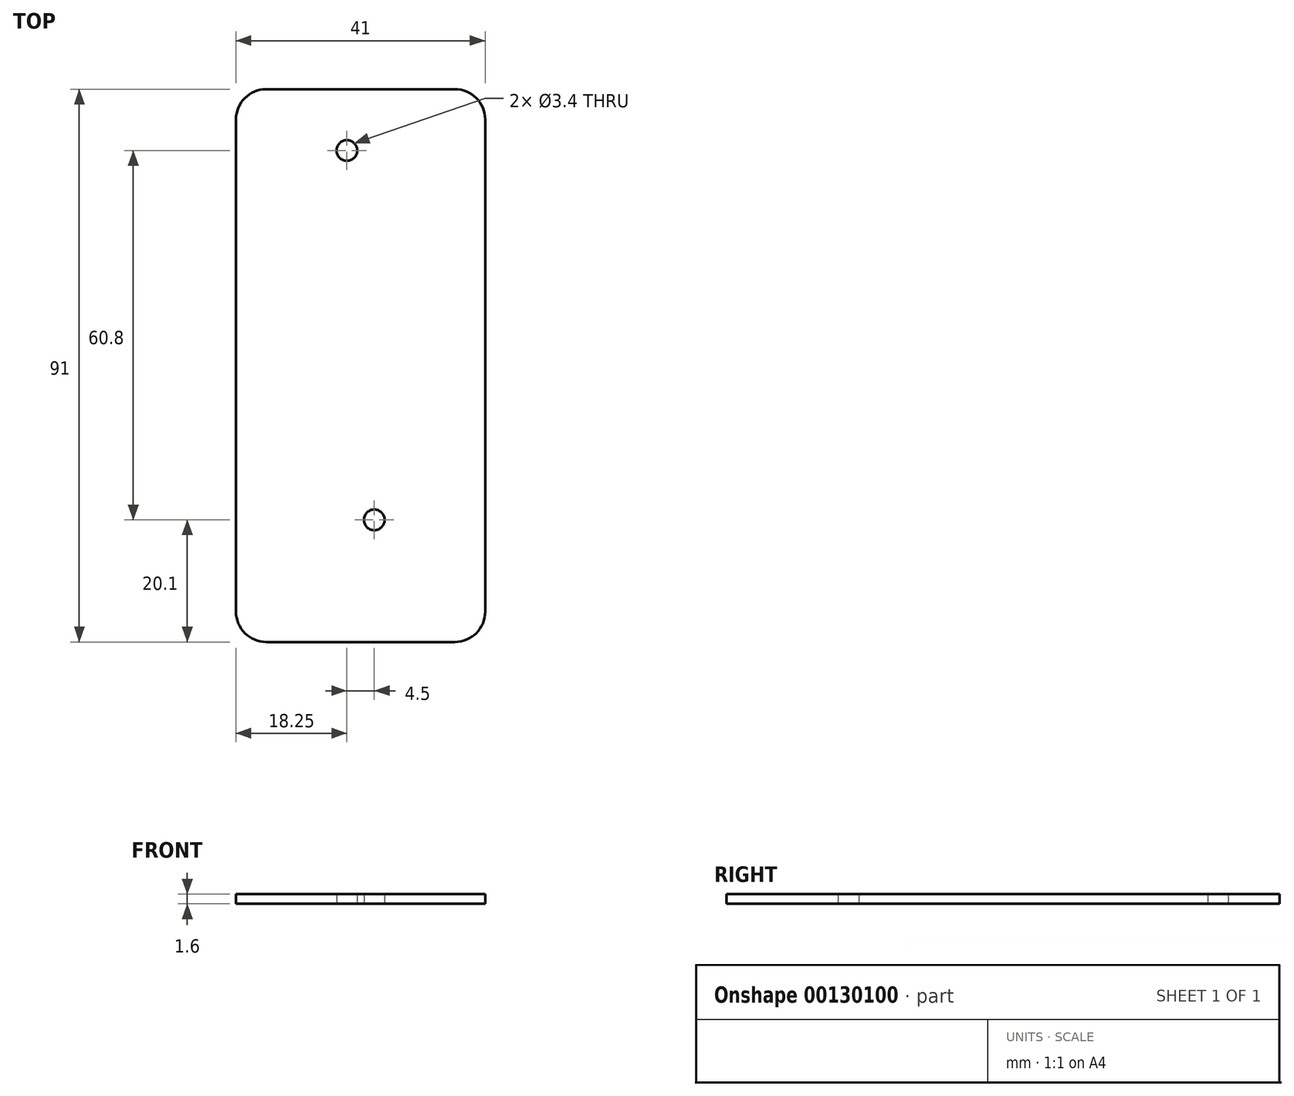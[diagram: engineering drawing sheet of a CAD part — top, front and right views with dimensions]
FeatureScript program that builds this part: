
annotation { "Feature Type Name" : "Feature", "Feature Type Description" : "" }
export const myFeature = defineFeature(function(context is Context, id is Id, definition is map)
    precondition{}
    {
        {
            var Q0;
            Q0=qCreatedBy(makeId("Top.planeOp"),FACE);
            var sketch = newSketch(context, id + "F0", { "sketchPlane" : qUnion([Q0])});
            skLineSegment(sketch, "E0.bottom", {"start": v(20.5, 45.5) * mm, "end": v(-20.5, 45.5) * mm});
            skLineSegment(sketch, "E0.top", {"start": v(20.5, -45.5) * mm, "end": v(-20.5, -45.5) * mm});
            skLineSegment(sketch, "E0.left", {"start": v(20.5, 45.5) * mm, "end": v(20.5, -45.5) * mm});
            skLineSegment(sketch, "E0.right", {"start": v(-20.5, 45.5) * mm, "end": v(-20.5, -45.5) * mm});
            skPoint(sketch, "E0.middle", {"position": v(0, 0) * mm});
            skLineSegment(sketch, "E1.bottom", {"start": v(-2.25, 35.4) * mm, "end": v(2.25, 35.4) * mm});
            skLineSegment(sketch, "E1.top", {"start": v(-2.25, -25.4) * mm, "end": v(2.25, -25.4) * mm});
            skLineSegment(sketch, "E1.left", {"start": v(-2.25, 35.4) * mm, "end": v(-2.25, -25.4) * mm});
            skLineSegment(sketch, "E1.right", {"start": v(2.25, 35.4) * mm, "end": v(2.25, -25.4) * mm});
            skCircle(sketch, "E2", {"center": v(-2.25, 35.4) * mm, "radius": 1.7 * mm});
            skCircle(sketch, "E3", {"center": v(2.25, -25.4) * mm, "radius": 1.7 * mm});
            skSolve(sketch);
        }
        {
            var Q0;
            Q0=makeQuery(id+"F0.imprint","IMPRINT",FACE,{"disambiguationData":[TD([[makeQuery(id+"F0.imprint","IMPRINT",EDGE,{"derivedFrom":sQuery(id+"F0.wireOp",EDGE,"E0.bottom")}),1.0]])]});
            var Q1;
            {var subQ0=sQuery(id+"F0.wireOp",EDGE,"E1.right");var subQ1=sQuery(id+"F0.wireOp",EDGE,"E1.bottom");var subQ2=makeQuery(id+"F0.imprint","INTERSECT",VERTEX,{"derivedFrom":[subQ1,subQ0]});Q1=makeQuery(id+"F0.imprint","IMPRINT",FACE,{"disambiguationData":[TD([[makeQuery(id+"F0.imprint","IMPRINT",EDGE,{"disambiguationData":[TD([[subQ2,1.0]])],"derivedFrom":subQ1}),-1.0]])]});}
            extrude(context, id + "F1", {"entities" : qUnion([Q0, Q1]), "depth" : 1.6 * mm});
        }
        {
            var Q0;
            Q0=makeQuery(id+"F1.opExtrude","SWEPT_EDGE",EDGE,{"disambiguationData":[OSD([sQuery(id+"F0.wireOp",EDGE,"E0.bottom"),sQuery(id+"F0.wireOp",EDGE,"E0.right")])]});
            var Q1;
            Q1=makeQuery(id+"F1.opExtrude","SWEPT_EDGE",EDGE,{"disambiguationData":[OSD([sQuery(id+"F0.wireOp",EDGE,"E0.bottom"),sQuery(id+"F0.wireOp",EDGE,"E0.left")])]});
            var Q2;
            Q2=makeQuery(id+"F1.opExtrude","SWEPT_EDGE",EDGE,{"disambiguationData":[OSD([sQuery(id+"F0.wireOp",EDGE,"E0.top"),sQuery(id+"F0.wireOp",EDGE,"E0.left")])]});
            var Q3;
            Q3=makeQuery(id+"F1.opExtrude","SWEPT_EDGE",EDGE,{"disambiguationData":[OSD([sQuery(id+"F0.wireOp",EDGE,"E0.top"),sQuery(id+"F0.wireOp",EDGE,"E0.right")])]});
            fillet(context, id + "F2", {"entities" : qUnion([Q0, Q1, Q2, Q3]), "radius" : 5 * mm, "tangentPropagation" : true, "allowEdgeOverflow" : false});
        }
    });
